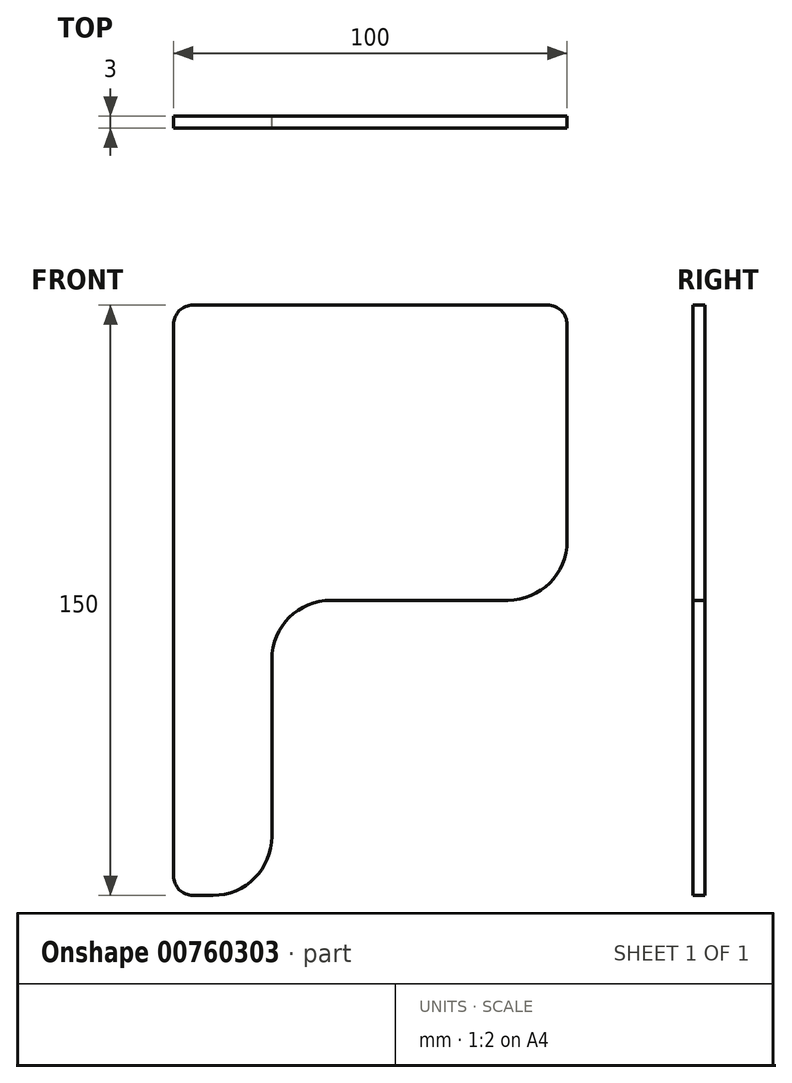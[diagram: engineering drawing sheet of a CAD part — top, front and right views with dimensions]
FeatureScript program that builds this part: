
annotation { "Feature Type Name" : "Feature", "Feature Type Description" : "" }
export const myFeature = defineFeature(function(context is Context, id is Id, definition is map)
    precondition{}
    {
        {
            var Q0;
            Q0=qCreatedBy(makeId("Front.planeOp"),FACE);
            var sketch = newSketch(context, id + "F0", { "sketchPlane" : qUnion([Q0])});
            skLineSegment(sketch, "E0.bottom", {"start": v(0, 0) * mm, "end": v(100, 0) * mm});
            skLineSegment(sketch, "E0.top", {"start": v(5, 150) * mm, "end": v(95, 150) * mm});
            skLineSegment(sketch, "E0.left", {"start": v(0, 0) * mm, "end": v(0, 145) * mm});
            skLineSegment(sketch, "E0.right", {"start": v(100, 0) * mm, "end": v(100, 145) * mm});
            skLineSegment(sketch, "E1.bottom", {"start": v(100, 0) * mm, "end": v(25, 0) * mm});
            skLineSegment(sketch, "E1.top", {"start": v(100, 75) * mm, "end": v(25, 75) * mm});
            skLineSegment(sketch, "E1.left", {"start": v(100, 0) * mm, "end": v(100, 75) * mm});
            skLineSegment(sketch, "E1.right", {"start": v(25, 0) * mm, "end": v(25, 75) * mm});
            skPoint(sketch, "E2.visualSharp", {"position": v(0, 150) * mm});
            skArc(sketch, "E2.filletArc", {"start": v(5, 150) * mm, "mid": v(1.46, 148.54) * mm, "end": v(0, 145) * mm});
            skPoint(sketch, "E3.visualSharp", {"position": v(100, 150) * mm});
            skArc(sketch, "E3.filletArc", {"start": v(100, 145) * mm, "mid": v(98.54, 148.54) * mm, "end": v(95, 150) * mm});
            skSolve(sketch);
        }
        {
            var Q0;
            Q0=makeQuery(id+"F0.imprint","IMPRINT",FACE,{"disambiguationData":[TD([[makeQuery(id+"F0.imprint","IMPRINT",EDGE,{"derivedFrom":sQuery(id+"F0.wireOp",EDGE,"E0.top")}),-1.0]])]});
            extrude(context, id + "F1", {"entities" : qUnion([Q0]), "depth" : 3 * mm, "offsetDistance" : 25 * mm});
        }
        {
            var Q0;
            Q0=makeQuery(id+"F1.opExtrude","SWEPT_EDGE",EDGE,{"disambiguationData":[OSD([sQuery(id+"F0.wireOp",EDGE,"E0.bottom"),sQuery(id+"F0.wireOp",EDGE,"E0.left")])]});
            fillet(context, id + "F2", {"entities" : qUnion([Q0]), "radius" : 5 * mm, "tangentPropagation" : true, "allowEdgeOverflow" : false});
        }
        {
            var Q0;
            Q0=makeQuery(id+"F1.opExtrude","SWEPT_EDGE",EDGE,{"disambiguationData":[OSD([sQuery(id+"F0.wireOp",EDGE,"E0.right"),sQuery(id+"F0.wireOp",EDGE,"E1.top")])]});
            fillet(context, id + "F3", {"entities" : qUnion([Q0]), "radius" : 15 * mm, "tangentPropagation" : true, "allowEdgeOverflow" : false});
        }
        {
            var Q0;
            Q0=makeQuery(id+"F1.opExtrude","SWEPT_EDGE",EDGE,{"disambiguationData":[OSD([sQuery(id+"F0.wireOp",EDGE,"E0.bottom"),sQuery(id+"F0.wireOp",EDGE,"E1.right")])]});
            fillet(context, id + "F4", {"entities" : qUnion([Q0]), "radius" : 15 * mm, "tangentPropagation" : true, "allowEdgeOverflow" : false});
        }
        {
            var Q0;
            Q0=makeQuery(id+"F1.opExtrude","SWEPT_EDGE",EDGE,{"disambiguationData":[OSD([sQuery(id+"F0.wireOp",EDGE,"E1.top"),sQuery(id+"F0.wireOp",EDGE,"E1.right")])]});
            fillet(context, id + "F5", {"entities" : qUnion([Q0]), "radius" : 15 * mm, "tangentPropagation" : true, "allowEdgeOverflow" : false});
        }
    });
